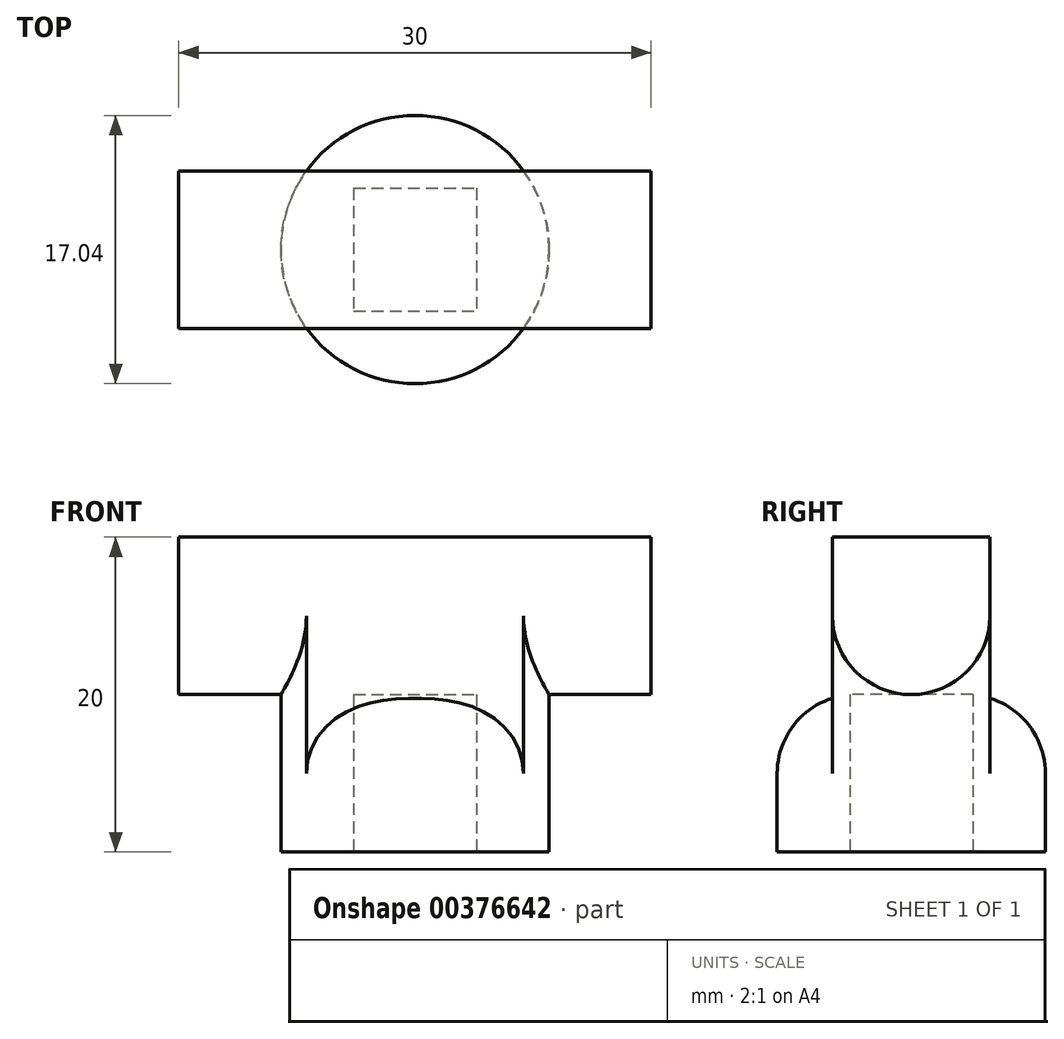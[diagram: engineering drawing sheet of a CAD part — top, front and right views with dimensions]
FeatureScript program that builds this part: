
annotation { "Feature Type Name" : "Feature", "Feature Type Description" : "" }
export const myFeature = defineFeature(function(context is Context, id is Id, definition is map)
    precondition{}
    {
        {
            var Q0;
            Q0=qCreatedBy(makeId("Top.planeOp"),FACE);
            var sketch = newSketch(context, id + "F0", { "sketchPlane" : qUnion([Q0])});
            skLineSegment(sketch, "E0.bottom", {"start": v(-3.9, 3.9) * mm, "end": v(3.9, 3.9) * mm});
            skLineSegment(sketch, "E0.top", {"start": v(-3.9, -3.9) * mm, "end": v(3.9, -3.9) * mm});
            skLineSegment(sketch, "E0.left", {"start": v(-3.9, 3.9) * mm, "end": v(-3.9, -3.9) * mm});
            skLineSegment(sketch, "E0.right", {"start": v(3.9, 3.9) * mm, "end": v(3.9, -3.9) * mm});
            skPoint(sketch, "E0.middle", {"position": v(0, 0) * mm});
            skCircle(sketch, "E1", {"center": v(0, 0) * mm, "radius": 5.52 * mm, "construction": true});
            skCircle(sketch, "E2.0", {"center": v(0, 0) * mm, "radius": 8.52 * mm});
            skSolve(sketch);
        }
        {
            var Q0;
            Q0 = qSketchRegion(id + "F0", true);
            extrude(context, id + "F1", {"entities" : qUnion([Q0]), "depth" : 10 * mm});
        }
        {
            var Q0;
            Q0=makeQuery(id+"F1.opExtrude","CAP_FACE",FACE,{"disambiguationData":[OSD([sQuery(id+"F0.wireOp",EDGE,"E0.bottom"),sQuery(id+"F0.wireOp",EDGE,"E0.top"),sQuery(id+"F0.wireOp",EDGE,"E0.left"),sQuery(id+"F0.wireOp",EDGE,"E0.right"),sQuery(id+"F0.wireOp",EDGE,"E2.0")])],"isStart":false});
            var sketch = newSketch(context, id + "F2", { "sketchPlane" : qUnion([Q0])});
            skLineSegment(sketch, "E3.bottom", {"start": v(-15, 5) * mm, "end": v(15, 5) * mm});
            skLineSegment(sketch, "E3.top", {"start": v(-15, -5) * mm, "end": v(15, -5) * mm});
            skLineSegment(sketch, "E3.left", {"start": v(-15, 5) * mm, "end": v(-15, -5) * mm});
            skLineSegment(sketch, "E3.right", {"start": v(15, 5) * mm, "end": v(15, -5) * mm});
            skPoint(sketch, "E3.middle", {"position": v(0, 0) * mm});
            skSolve(sketch);
        }
        {
            var Q0;
            {var subQ0=sQuery(id+"F2.wireOp",EDGE,"E3.left");Q0=makeQuery(id+"F2.imprint","IMPRINT",FACE,{"disambiguationData":[TD([[makeQuery(id+"F2.imprint","IMPRINT",EDGE,{"derivedFrom":subQ0}),1.0]])]});}
            var Q1;
            {var subQ1=makeQuery(id+"F1.opExtrude","CAP_EDGE",EDGE,{"disambiguationData":[OSD([sQuery(id+"F0.wireOp",EDGE,"E0.left")])],"isStart":false});Q1=makeQuery(id+"F2.imprint","IMPRINT",FACE,{"disambiguationData":[TD([[makeQuery(id+"F2.imprint","IMPRINT",EDGE,{"derivedFrom":subQ1}),-1.0]])]});}
            var Q2;
            {var subQ1=makeQuery(id+"F1.opExtrude","CAP_EDGE",EDGE,{"disambiguationData":[OSD([sQuery(id+"F0.wireOp",EDGE,"E0.left")])],"isStart":false});Q2=makeQuery(id+"F2.imprint","IMPRINT",FACE,{"disambiguationData":[TD([[makeQuery(id+"F2.imprint","IMPRINT",EDGE,{"derivedFrom":subQ1}),1.0]])]});}
            var Q3;
            {var subQ1=makeQuery(id+"F1.opExtrude","CAP_EDGE",EDGE,{"disambiguationData":[OSD([sQuery(id+"F0.wireOp",EDGE,"E0.right")])],"isStart":false});Q3=makeQuery(id+"F2.imprint","IMPRINT",FACE,{"disambiguationData":[TD([[makeQuery(id+"F2.imprint","IMPRINT",EDGE,{"derivedFrom":subQ1}),1.0]])]});}
            var Q4;
            {var subQ0=sQuery(id+"F2.wireOp",EDGE,"E3.right");Q4=makeQuery(id+"F2.imprint","IMPRINT",FACE,{"disambiguationData":[TD([[makeQuery(id+"F2.imprint","IMPRINT",EDGE,{"derivedFrom":subQ0}),-1.0]])]});}
            extrude(context, id + "F3", {"entities" : qUnion([Q0, Q1, Q2, Q3, Q4]), "operationType" : NewBodyOperationType.ADD, "depth" : 10 * mm});
        }
        {
            var Q0;
            {var subQ0=sQuery(id+"F2.wireOp",EDGE,"E3.top");Q0=makeQuery(id+"F3.boolean.opBoolean","SPLIT",EDGE,{"disambiguationData":[topologyDisambiguationEdgeConnected([makeQuery(id+"F1.opExtrude","CAP_FACE",FACE,{"disambiguationData":[OSD([sQuery(id+"F0.wireOp",EDGE,"E0.bottom"),sQuery(id+"F0.wireOp",EDGE,"E0.top"),sQuery(id+"F0.wireOp",EDGE,"E0.left"),sQuery(id+"F0.wireOp",EDGE,"E0.right"),sQuery(id+"F0.wireOp",EDGE,"E2.0")])],"isStart":false}),makeQuery(id+"F3.opExtrude","SWEPT_FACE",FACE,{"disambiguationData":[OSD([subQ0])]})])],"derivedFrom":makeQuery(id+"F3.opExtrude","CAP_EDGE",EDGE,{"disambiguationData":[OSD([subQ0])],"isStart":true})});}
            var Q1;
            {var subQ0=sQuery(id+"F2.wireOp",EDGE,"E3.bottom");Q1=makeQuery(id+"F3.boolean.opBoolean","SPLIT",EDGE,{"disambiguationData":[topologyDisambiguationEdgeConnected([makeQuery(id+"F1.opExtrude","CAP_FACE",FACE,{"disambiguationData":[OSD([sQuery(id+"F0.wireOp",EDGE,"E0.bottom"),sQuery(id+"F0.wireOp",EDGE,"E0.top"),sQuery(id+"F0.wireOp",EDGE,"E0.left"),sQuery(id+"F0.wireOp",EDGE,"E0.right"),sQuery(id+"F0.wireOp",EDGE,"E2.0")])],"isStart":false}),makeQuery(id+"F3.opExtrude","SWEPT_FACE",FACE,{"disambiguationData":[OSD([subQ0])]})])],"derivedFrom":makeQuery(id+"F3.opExtrude","CAP_EDGE",EDGE,{"disambiguationData":[OSD([subQ0])],"isStart":true})});}
            fillet(context, id + "F4", {"entities" : qUnion([Q0, Q1]), "radius" : 5 * mm, "tangentPropagation" : true, "allowEdgeOverflow" : false});
        }
        {
            var Q0;
            {var subQ0=sQuery(id+"F0.wireOp",EDGE,"E2.0");Q0=makeQuery(id+"F3.boolean.opBoolean","SPLIT",EDGE,{"disambiguationData":[topologyDisambiguationEdgeConnected([makeQuery(id+"F1.opExtrude","SWEPT_FACE",FACE,{"disambiguationData":[OSD([subQ0])]}),makeQuery(id+"F3.opExtrude","CAP_FACE",FACE,{"disambiguationData":[OSD([sQuery(id+"F2.wireOp",EDGE,"E3.bottom"),sQuery(id+"F2.wireOp",EDGE,"E3.top"),sQuery(id+"F2.wireOp",EDGE,"E3.left"),sQuery(id+"F2.wireOp",EDGE,"E3.right")])],"isStart":true})]),OD(0.0)],"derivedFrom":makeQuery(id+"F1.opExtrude","CAP_EDGE",EDGE,{"disambiguationData":[OSD([subQ0])],"isStart":false})});}
            var Q1;
            {var subQ0=sQuery(id+"F0.wireOp",EDGE,"E2.0");Q1=makeQuery(id+"F3.boolean.opBoolean","SPLIT",EDGE,{"disambiguationData":[topologyDisambiguationEdgeConnected([makeQuery(id+"F1.opExtrude","SWEPT_FACE",FACE,{"disambiguationData":[OSD([subQ0])]}),makeQuery(id+"F3.opExtrude","CAP_FACE",FACE,{"disambiguationData":[OSD([sQuery(id+"F2.wireOp",EDGE,"E3.bottom"),sQuery(id+"F2.wireOp",EDGE,"E3.top"),sQuery(id+"F2.wireOp",EDGE,"E3.left"),sQuery(id+"F2.wireOp",EDGE,"E3.right")])],"isStart":true})]),OD(1.0)],"derivedFrom":makeQuery(id+"F1.opExtrude","CAP_EDGE",EDGE,{"disambiguationData":[OSD([subQ0])],"isStart":false})});}
            fillet(context, id + "F5", {"entities" : qUnion([Q0, Q1]), "radius" : 5 * mm, "tangentPropagation" : true, "allowEdgeOverflow" : false});
        }
    });
